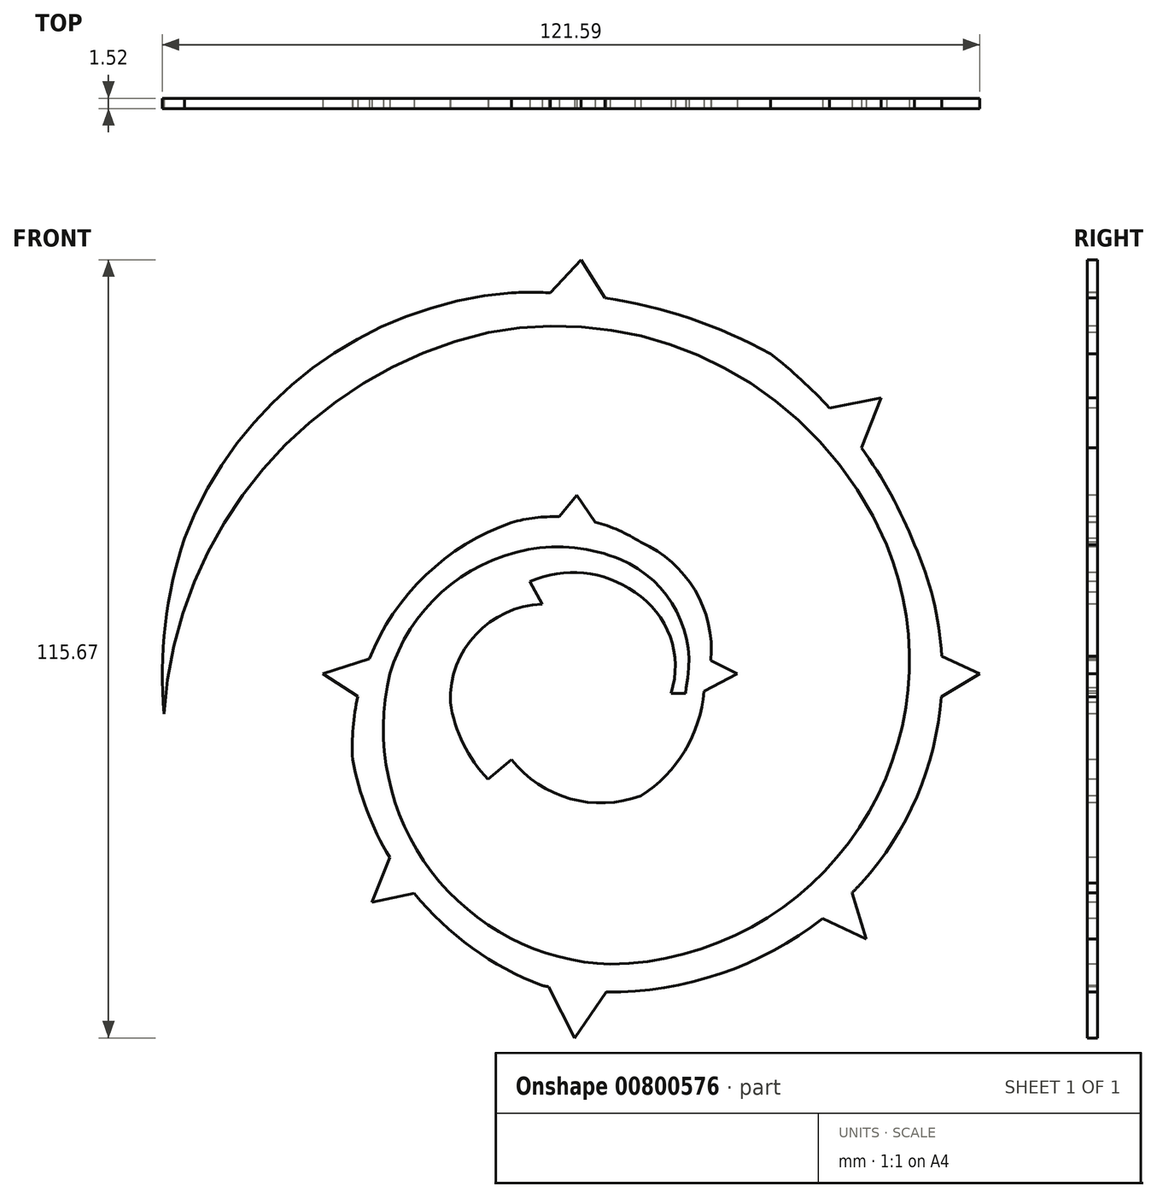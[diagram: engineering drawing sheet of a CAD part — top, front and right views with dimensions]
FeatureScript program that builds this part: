
annotation { "Feature Type Name" : "Feature", "Feature Type Description" : "" }
export const myFeature = defineFeature(function(context is Context, id is Id, definition is map)
    precondition{}
    {
        {
            var Q0;
            Q0=qCreatedBy(makeId("Front.planeOp"),FACE);
            var sketch = newSketch(context, id + "F0", { "sketchPlane" : qUnion([Q0])});
            skArc(sketch, "E0", {"start": v(-17.42, 47.63) * mm, "mid": v(-50.98, 27.27) * mm, "end": v(-65.7, -9.12) * mm});
            skArc(sketch, "E1", {"start": v(41.79, 16.06) * mm, "mid": v(17.76, 42.3) * mm, "end": v(-17.42, 47.63) * mm});
            skArc(sketch, "E2", {"start": v(0.68, -46.33) * mm, "mid": v(37.74, -26) * mm, "end": v(41.79, 16.06) * mm});
            skArc(sketch, "E3", {"start": v(-32.1, -3.14) * mm, "mid": v(-25.95, -32.51) * mm, "end": v(0.68, -46.33) * mm});
            skArc(sketch, "E4", {"start": v(-11.55, 15.33) * mm, "mid": v(-24.43, 8.98) * mm, "end": v(-32.1, -3.14) * mm});
            skArc(sketch, "E5", {"start": v(11.94, -5.22) * mm, "mid": v(10.56, 6.12) * mm, "end": v(2.15, 13.86) * mm});
            skArc(sketch, "E6", {"start": v(2.15, 13.86) * mm, "mid": v(-4.6, 15.6) * mm, "end": v(-11.55, 15.33) * mm});
            skLineSegment(sketch, "E7", {"start": v(9.72, -6.06) * mm, "end": v(11.9, -6.06) * mm});
            skLineSegment(sketch, "E8", {"start": v(11.9, -6.06) * mm, "end": v(11.94, -5.22) * mm});
            skArc(sketch, "E9", {"start": v(9.72, -6.06) * mm, "mid": v(9.59, 2.4) * mm, "end": v(4.34, 9.02) * mm});
            skArc(sketch, "E10", {"start": v(4.34, 9.02) * mm, "mid": v(-3.26, 11.84) * mm, "end": v(-11.25, 10.56) * mm});
            skLineSegment(sketch, "E11", {"start": v(-11.25, 10.56) * mm, "end": v(-9.46, 7.22) * mm});
            skArc(sketch, "E12", {"start": v(-9.46, 7.22) * mm, "mid": v(-19.31, 2.73) * mm, "end": v(-23.12, -7.4) * mm});
            skArc(sketch, "E13", {"start": v(-23.12, -7.4) * mm, "mid": v(-21.19, -13.55) * mm, "end": v(-17.48, -18.83) * mm});
            skLineSegment(sketch, "E14", {"start": v(-14.01, -15.88) * mm, "end": v(-17.48, -18.83) * mm});
            skArc(sketch, "E15", {"start": v(-14.01, -15.88) * mm, "mid": v(-5.27, -21.7) * mm, "end": v(5.23, -21.26) * mm});
            skArc(sketch, "E16", {"start": v(5.23, -21.26) * mm, "mid": v(11.77, -14.62) * mm, "end": v(14.6, -5.74) * mm});
            skArc(sketch, "E17", {"start": v(14.6, -5.74) * mm, "mid": v(14.34, 7.2) * mm, "end": v(5.23, 16.4) * mm});
            skArc(sketch, "E18", {"start": v(-14.01, 53.52) * mm, "mid": v(-43.6, 42.3) * mm, "end": v(-62.64, 17.02) * mm});
            skArc(sketch, "E19", {"start": v(5.23, 16.4) * mm, "mid": v(-4.07, 19.95) * mm, "end": v(-14.01, 19.35) * mm});
            skArc(sketch, "E20", {"start": v(-14.01, 19.35) * mm, "mid": v(-31.7, 5.68) * mm, "end": v(-37.65, -15.88) * mm});
            skArc(sketch, "E21", {"start": v(-37.65, -15.88) * mm, "mid": v(-27.95, -36.37) * mm, "end": v(-9.46, -49.48) * mm});
            skArc(sketch, "E22", {"start": v(-9.46, -49.48) * mm, "mid": v(16.27, -47.98) * mm, "end": v(38.06, -34.24) * mm});
            skArc(sketch, "E23", {"start": v(38.06, -34.24) * mm, "mid": v(49.49, -10.26) * mm, "end": v(45.93, 16.06) * mm});
            skArc(sketch, "E24", {"start": v(45.93, 16.06) * mm, "mid": v(37.16, 31.69) * mm, "end": v(24.54, 44.42) * mm});
            skArc(sketch, "E25", {"start": v(24.54, 44.42) * mm, "mid": v(5.89, 51.6) * mm, "end": v(-14.01, 53.52) * mm});
            skLineSegment(sketch, "E26", {"start": v(-0.1, 52.75) * mm, "end": v(-3.65, 58.4) * mm});
            skLineSegment(sketch, "E27", {"start": v(-3.65, 58.4) * mm, "end": v(-8.23, 53.52) * mm});
            skLineSegment(sketch, "E28", {"start": v(33.29, 36.37) * mm, "end": v(40.96, 37.92) * mm});
            skLineSegment(sketch, "E29", {"start": v(40.96, 37.92) * mm, "end": v(38.05, 30.48) * mm});
            skLineSegment(sketch, "E30", {"start": v(49.98, -0.54) * mm, "end": v(55.64, -3.14) * mm});
            skLineSegment(sketch, "E31", {"start": v(55.64, -3.14) * mm, "end": v(49.91, -6.57) * mm});
            skLineSegment(sketch, "E32", {"start": v(36.65, -35.68) * mm, "end": v(38.76, -42.58) * mm});
            skLineSegment(sketch, "E33", {"start": v(38.76, -42.58) * mm, "end": v(32.25, -39.53) * mm});
            skLineSegment(sketch, "E34", {"start": v(-8.52, -49.66) * mm, "end": v(-4.63, -57.27) * mm});
            skLineSegment(sketch, "E35", {"start": v(-4.63, -57.27) * mm, "end": v(0.06, -50.45) * mm});
            skLineSegment(sketch, "E36", {"start": v(-35.18, -0.93) * mm, "end": v(-42.07, -3.14) * mm});
            skLineSegment(sketch, "E37", {"start": v(-42.07, -3.14) * mm, "end": v(-36.89, -6.49) * mm});
            skLineSegment(sketch, "E38", {"start": v(-32.14, -30.46) * mm, "end": v(-34.77, -37.07) * mm});
            skLineSegment(sketch, "E39", {"start": v(-34.77, -37.07) * mm, "end": v(-28.46, -35.74) * mm});
            skLineSegment(sketch, "E40", {"start": v(-6.92, 20.21) * mm, "end": v(-4.3, 23.4) * mm});
            skLineSegment(sketch, "E41", {"start": v(-4.3, 23.4) * mm, "end": v(-1.6, 19.44) * mm});
            skLineSegment(sketch, "E42", {"start": v(15.65, -1.14) * mm, "end": v(19.58, -3.14) * mm});
            skLineSegment(sketch, "E43", {"start": v(19.58, -3.14) * mm, "end": v(14.6, -5.74) * mm});
            skArc(sketch, "E44", {"start": v(-62.64, 17.02) * mm, "mid": v(-65.5, 4.1) * mm, "end": v(-65.7, -9.12) * mm});
            skSolve(sketch);
        }
        {
            var Q0;
            Q0=makeQuery(id+"F0.imprint","IMPRINT",FACE,{"disambiguationData":[TD([[makeQuery(id+"F0.imprint","IMPRINT",EDGE,{"derivedFrom":sQuery(id+"F0.wireOp",EDGE,"E0")}),-1.0]])]});
            var Q1;
            {var subQ0=sQuery(id+"F0.wireOp",EDGE,"E40");Q1=makeQuery(id+"F0.imprint","IMPRINT",FACE,{"disambiguationData":[TD([[makeQuery(id+"F0.imprint","IMPRINT",EDGE,{"derivedFrom":subQ0}),-1.0]])]});}
            var Q2;
            {var subQ2=sQuery(id+"F0.wireOp",EDGE,"E42");Q2=makeQuery(id+"F0.imprint","IMPRINT",FACE,{"disambiguationData":[TD([[makeQuery(id+"F0.imprint","IMPRINT",EDGE,{"derivedFrom":subQ2}),-1.0]])]});}
            var Q3;
            {var subQ0=sQuery(id+"F0.wireOp",EDGE,"E36");Q3=makeQuery(id+"F0.imprint","IMPRINT",FACE,{"disambiguationData":[TD([[makeQuery(id+"F0.imprint","IMPRINT",EDGE,{"derivedFrom":subQ0}),1.0]])]});}
            var Q4;
            {var subQ0=sQuery(id+"F0.wireOp",EDGE,"E38");Q4=makeQuery(id+"F0.imprint","IMPRINT",FACE,{"disambiguationData":[TD([[makeQuery(id+"F0.imprint","IMPRINT",EDGE,{"derivedFrom":subQ0}),1.0]])]});}
            var Q5;
            {var subQ0=sQuery(id+"F0.wireOp",EDGE,"E34");Q5=makeQuery(id+"F0.imprint","IMPRINT",FACE,{"disambiguationData":[TD([[makeQuery(id+"F0.imprint","IMPRINT",EDGE,{"derivedFrom":subQ0}),1.0]])]});}
            var Q6;
            {var subQ0=sQuery(id+"F0.wireOp",EDGE,"E32");Q6=makeQuery(id+"F0.imprint","IMPRINT",FACE,{"disambiguationData":[TD([[makeQuery(id+"F0.imprint","IMPRINT",EDGE,{"derivedFrom":subQ0}),-1.0]])]});}
            var Q7;
            {var subQ0=sQuery(id+"F0.wireOp",EDGE,"E30");Q7=makeQuery(id+"F0.imprint","IMPRINT",FACE,{"disambiguationData":[TD([[makeQuery(id+"F0.imprint","IMPRINT",EDGE,{"derivedFrom":subQ0}),-1.0]])]});}
            var Q8;
            {var subQ0=sQuery(id+"F0.wireOp",EDGE,"E28");Q8=makeQuery(id+"F0.imprint","IMPRINT",FACE,{"disambiguationData":[TD([[makeQuery(id+"F0.imprint","IMPRINT",EDGE,{"derivedFrom":subQ0}),-1.0]])]});}
            var Q9;
            {var subQ0=sQuery(id+"F0.wireOp",EDGE,"E26");Q9=makeQuery(id+"F0.imprint","IMPRINT",FACE,{"disambiguationData":[TD([[makeQuery(id+"F0.imprint","IMPRINT",EDGE,{"derivedFrom":subQ0}),1.0]])]});}
            var Q10;
            Q10=sQuery(id+"F0.wireOp",EDGE,"E0");
            var Q11;
            Q11=sQuery(id+"F0.wireOp",EDGE,"E1");
            var Q12;
            Q12=sQuery(id+"F0.wireOp",EDGE,"E2");
            var Q13;
            Q13=sQuery(id+"F0.wireOp",EDGE,"E3");
            var Q14;
            Q14=sQuery(id+"F0.wireOp",EDGE,"E4");
            var Q15;
            Q15=sQuery(id+"F0.wireOp",EDGE,"E5");
            var Q16;
            Q16=sQuery(id+"F0.wireOp",EDGE,"E6");
            var Q17;
            Q17=sQuery(id+"F0.wireOp",EDGE,"E7");
            var Q18;
            Q18=sQuery(id+"F0.wireOp",EDGE,"E8");
            var Q19;
            Q19=sQuery(id+"F0.wireOp",EDGE,"E9");
            var Q20;
            Q20=sQuery(id+"F0.wireOp",EDGE,"E10");
            var Q21;
            Q21=sQuery(id+"F0.wireOp",EDGE,"E11");
            var Q22;
            Q22=sQuery(id+"F0.wireOp",EDGE,"E12");
            var Q23;
            Q23=sQuery(id+"F0.wireOp",EDGE,"E13");
            var Q24;
            Q24=sQuery(id+"F0.wireOp",EDGE,"E14");
            var Q25;
            Q25=sQuery(id+"F0.wireOp",EDGE,"E15");
            var Q26;
            Q26=sQuery(id+"F0.wireOp",EDGE,"E16");
            var Q27;
            Q27=sQuery(id+"F0.wireOp",EDGE,"E17");
            var Q28;
            Q28=sQuery(id+"F0.wireOp",EDGE,"E18");
            var Q29;
            Q29=sQuery(id+"F0.wireOp",EDGE,"E19");
            var Q30;
            Q30=sQuery(id+"F0.wireOp",EDGE,"E20");
            var Q31;
            Q31=sQuery(id+"F0.wireOp",EDGE,"E21");
            var Q32;
            Q32=sQuery(id+"F0.wireOp",EDGE,"E22");
            var Q33;
            Q33=sQuery(id+"F0.wireOp",EDGE,"E23");
            var Q34;
            Q34=sQuery(id+"F0.wireOp",EDGE,"E24");
            var Q35;
            Q35=sQuery(id+"F0.wireOp",EDGE,"E25");
            var Q36;
            Q36=sQuery(id+"F0.wireOp",EDGE,"E26");
            var Q37;
            Q37=sQuery(id+"F0.wireOp",EDGE,"E27");
            var Q38;
            Q38=sQuery(id+"F0.wireOp",EDGE,"E28");
            var Q39;
            Q39=sQuery(id+"F0.wireOp",EDGE,"E29");
            var Q40;
            Q40=sQuery(id+"F0.wireOp",EDGE,"E30");
            var Q41;
            Q41=sQuery(id+"F0.wireOp",EDGE,"E31");
            var Q42;
            Q42=sQuery(id+"F0.wireOp",EDGE,"E32");
            var Q43;
            Q43=sQuery(id+"F0.wireOp",EDGE,"E33");
            var Q44;
            Q44=sQuery(id+"F0.wireOp",EDGE,"E34");
            var Q45;
            Q45=sQuery(id+"F0.wireOp",EDGE,"E35");
            var Q46;
            Q46=sQuery(id+"F0.wireOp",EDGE,"E36");
            var Q47;
            Q47=sQuery(id+"F0.wireOp",EDGE,"E37");
            var Q48;
            Q48=sQuery(id+"F0.wireOp",EDGE,"E38");
            var Q49;
            Q49=sQuery(id+"F0.wireOp",EDGE,"E39");
            var Q50;
            Q50=sQuery(id+"F0.wireOp",EDGE,"E40");
            var Q51;
            Q51=sQuery(id+"F0.wireOp",EDGE,"E41");
            var Q52;
            Q52=sQuery(id+"F0.wireOp",EDGE,"E42");
            var Q53;
            Q53=sQuery(id+"F0.wireOp",EDGE,"E43");
            var Q54;
            Q54=sQuery(id+"F0.wireOp",EDGE,"E44");
            extrude(context, id + "F1", {"entities" : qUnion([Q0, Q1, Q2, Q3, Q4, Q5, Q6, Q7, Q8, Q9]), "surfaceEntities" : qUnion([Q10, Q11, Q12, Q13, Q14, Q15, Q16, Q17, Q18, Q19, Q20, Q21, Q22, Q23, Q24, Q25, Q26, Q27, Q28, Q29, Q30, Q31, Q32, Q33, Q34, Q35, Q36, Q37, Q38, Q39, Q40, Q41, Q42, Q43, Q44, Q45, Q46, Q47, Q48, Q49, Q50, Q51, Q52, Q53, Q54]), "oppositeDirection" : true, "depth" : 1.52 * mm, "offsetDistance" : 25.4 * mm});
        }
    });
